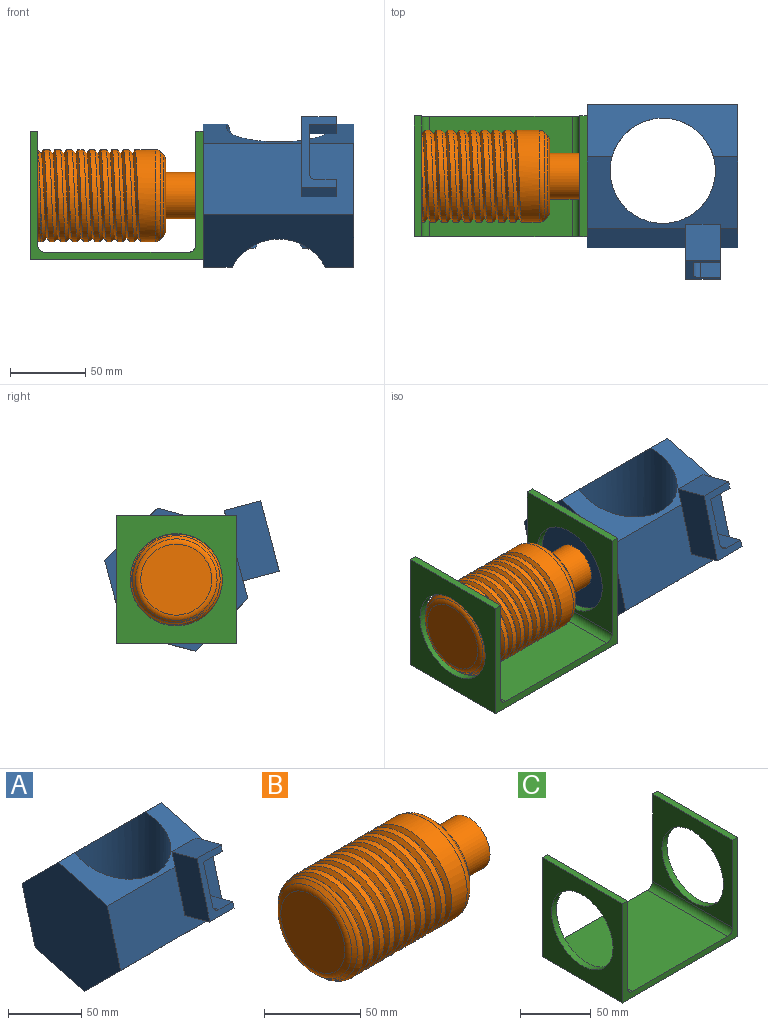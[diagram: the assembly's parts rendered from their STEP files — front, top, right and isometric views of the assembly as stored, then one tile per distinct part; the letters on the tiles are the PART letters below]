
ASSEMBLY  parts=3 mates=2
PART A: 21 faces, bbox 100x116.1x100 mm
  f0: plane 100x47.58mm, normal (0,-0.97,0.26), area 4644.8mm2, adj f2,f7,f8,f9,f10,f14,f15,f16
  f1: cylinder r=35mm len=95.16mm, axis (0,0,1), area 16030.8mm2, adj f2,f3,f4,f5,f6,f7
  f2: plane 100x47.58mm, normal (0,-0.26,0.97), area 2277.2mm2, adj f0,f1,f3,f8,f9,f20
  f3: plane 100x34.83mm, normal (0,0.71,0.71), area 3101.1mm2, adj f1,f2,f4,f8,f9
  f4: plane 100x47.58mm, normal (0,0.97,-0.26), area 4617.1mm2, adj f1,f3,f5,f6,f8,f9
  f5: plane 47.58x34.08mm, normal (0,0.26,-0.97), area 931.4mm2, adj f1,f4,f7,f8
  f6: plane 47.58x34.37mm, normal (0,0.26,-0.97), area 945.6mm2, adj f1,f4,f7,f9
  f7: plane 100x34.83mm, normal (0,-0.71,-0.71), area 3760.6mm2, adj f0,f1,f5,f6,f8,f9
  f8: plane 95.16x95.16mm, normal (1,0,0), area 6303.6mm2, adj f0,f2,f3,f4,f5,f7
  f9: plane 95.16x95.16mm, normal (-1,0,0), area 6303.6mm2, adj f0,f2,f3,f4,f6,f7
  f10: plane 38.73x32.79mm, normal (1,0,0), area 834.9mm2, adj f0,f11,f18,f19,f20
  f11: plane 24.15x18.21mm, normal (0,-0.26,-0.97), area 455.4mm2, adj f10,f12,f19,f20
  f12: plane 25.44x11.3mm, normal (1,0,0), area 125mm2, adj f11,f13,f19,f20
  f13: plane 24.15x23.21mm, normal (0,0.26,0.97), area 580.4mm2, adj f12,f14,f19,f20
  f14: plane 53.22x36.67mm, normal (-1,0,0), area 1209.9mm2, adj f0,f13,f15,f19,f20
  f15: plane 24.15x23.21mm, normal (0,-0.26,-0.97), area 580.4mm2, adj f0,f14,f16,f19
  f16: plane 25.44x11.3mm, normal (1,0,0), area 125mm2, adj f0,f15,f17,f19
  f17: plane 24.15x13.21mm, normal (0,0.26,0.97), area 330.4mm2, adj f0,f16,f18,f19
  f18: cylinder r=5mm len=25.44mm, axis (0,0.97,-0.26), area 196.3mm2, adj f0,f10,f17,f19
  f19: plane 46.75x23.21mm, normal (0,-0.97,0.26), area 429.5mm2, adj f10,f11,f12,f13,f14,f15,f16,f17
  f20: plane 23.21x11.12mm, normal (0,0.97,-0.26), area 148.6mm2, adj f2,f10,f11,f12,f13,f14
PART B: 23 faces, bbox 117x66.4x66.4 mm
  f0: cylinder r=30.66mm len=61.32mm, axis (1,0,0), area 2369.7mm2, adj f1,f16,f20,f21,f22
  f1: cylinder r=30.66mm len=61.32mm, axis (1,0,0), area 660.5mm2, adj f0,f2,f21,f22
  f2: cylinder r=30.66mm len=61.32mm, axis (1,0,0), area 660.7mm2, adj f1,f3,f21,f22
  f3: cylinder r=30.66mm len=61.32mm, axis (1,0,0), area 660.6mm2, adj f2,f4,f21,f22
  f4: cylinder r=30.66mm len=61.32mm, axis (1,0,0), area 660.7mm2, adj f3,f5,f21,f22
  f5: cylinder r=30.66mm len=61.32mm, axis (1,0,0), area 660.8mm2, adj f4,f6,f21,f22
  f6: cylinder r=30.66mm len=61.32mm, axis (1,0,0), area 660.6mm2, adj f5,f7,f21,f22
  f7: cylinder r=30.66mm len=61.32mm, axis (1,0,0), area 660.8mm2, adj f6,f8,f21,f22
  f8: cylinder r=30.66mm len=61.32mm, axis (1,0,0), area 611.9mm2, adj f7,f9,f17,f21,f22
  f9: cylinder r=30.66mm len=28.75mm, axis (1,0,0), area 27.4mm2, adj f8,f17,f21
  f10: cylinder r=15.43mm len=30.86mm, axis (1,0,0), area 2423.9mm2, adj f11,f13
  f11: plane 30.86x30.86mm, normal (1,0,0), area 748.1mm2, adj f10
  f12: plane 47.18x47.18mm, normal (-1,0,0), area 1748.3mm2, adj f18
  f13: plane 47.18x47.18mm, normal (1,0,0), area 1000.3mm2, adj f10,f19
  f14: cone r=30.66mm half-angle=45deg, axis (-1,0,0), area 518.3mm2, adj f16,f19
  f15: cone r=25.66mm half-angle=45deg, axis (1,0,0), area 488.7mm2, adj f17,f18,f21,f22
  f16: torus R=25.66mm, axis (1,0,0), area 744.2mm2, adj f0,f14
  f17: torus R=25.66mm, axis (-1,0,0), area 455.4mm2, adj f8,f9,f15,f21,f22
  f18: torus R=23.59mm, axis (-1,0,0), area 628.1mm2, adj f12,f15
  f19: torus R=23.59mm, axis (-1,0,0), area 628.1mm2, adj f13,f14
  f20: plane 4.16x2.49mm, normal (0,0,-1), area 5.2mm2, adj f0,f21,f22
  f21: bspline ~75.48x65.43mm, area 5711.8mm2, adj f0,f1,f2,f3,f4,f5,f6,f7
  f22: bspline ~74.34x65.43mm, area 5207.4mm2, adj f0,f1,f2,f3,f4,f5,f6,f7
PART C: 14 faces, bbox 115x80x85.5 mm
  f0: cylinder r=5mm len=80mm, axis (0,1,0), area 628.3mm2, adj f1,f9,f10,f11
  f1: plane 95.02x80mm, normal (0,0,1), area 7601.5mm2, adj f0,f2,f10,f11
  f2: cylinder r=5mm len=80mm, axis (0,1,0), area 628.3mm2, adj f1,f3,f10,f11
  f3: plane 80x75.52mm, normal (1,0,0), area 3087.7mm2, adj f2,f4,f10,f11,f13
  f4: plane 80x5mm, normal (0,0,1), area 400mm2, adj f3,f5,f10,f11
  f5: plane 85.52x80mm, normal (-1,0,0), area 3887.7mm2, adj f4,f6,f10,f11,f13
  f6: plane 115.02x80mm, normal (0,0,-1), area 9201.5mm2, adj f5,f7,f10,f11
  f7: plane 85.52x80mm, normal (1,0,0), area 3887.7mm2, adj f6,f8,f10,f11,f12
  f8: plane 80x5mm, normal (0,0,1), area 400mm2, adj f7,f9,f10,f11
  f9: plane 80x75.52mm, normal (-1,0,0), area 3087.7mm2, adj f0,f8,f10,f11,f12
  f10: plane 115.02x85.52mm, normal (0,-1,0), area 1391mm2, adj f0,f1,f2,f3,f4,f5,f6,f7
  f11: plane 115.02x85.52mm, normal (0,1,0), area 1391mm2, adj f0,f1,f2,f3,f4,f5,f6,f7
  f12: cylinder r=30.66mm len=61.32mm, axis (1,0,0), area 963.3mm2, adj f7,f9
  f13: cylinder r=30.66mm len=61.32mm, axis (1,0,0), area 963.3mm2, adj f3,f5
PLACE A t=(60.1,-90,82.07)mm
PLACE B t=(60.1,-90,82.07)mm
PLACE C t=(52.2,0,0)mm
MATE fastened B.f0 <-> A.f9  axis (1,0,0) through (60.1,-40,32.07)mm
MATE fastened A.f9 <-> C.f12  axis (-1,0,0) through (60.1,-40,32.07)mm
